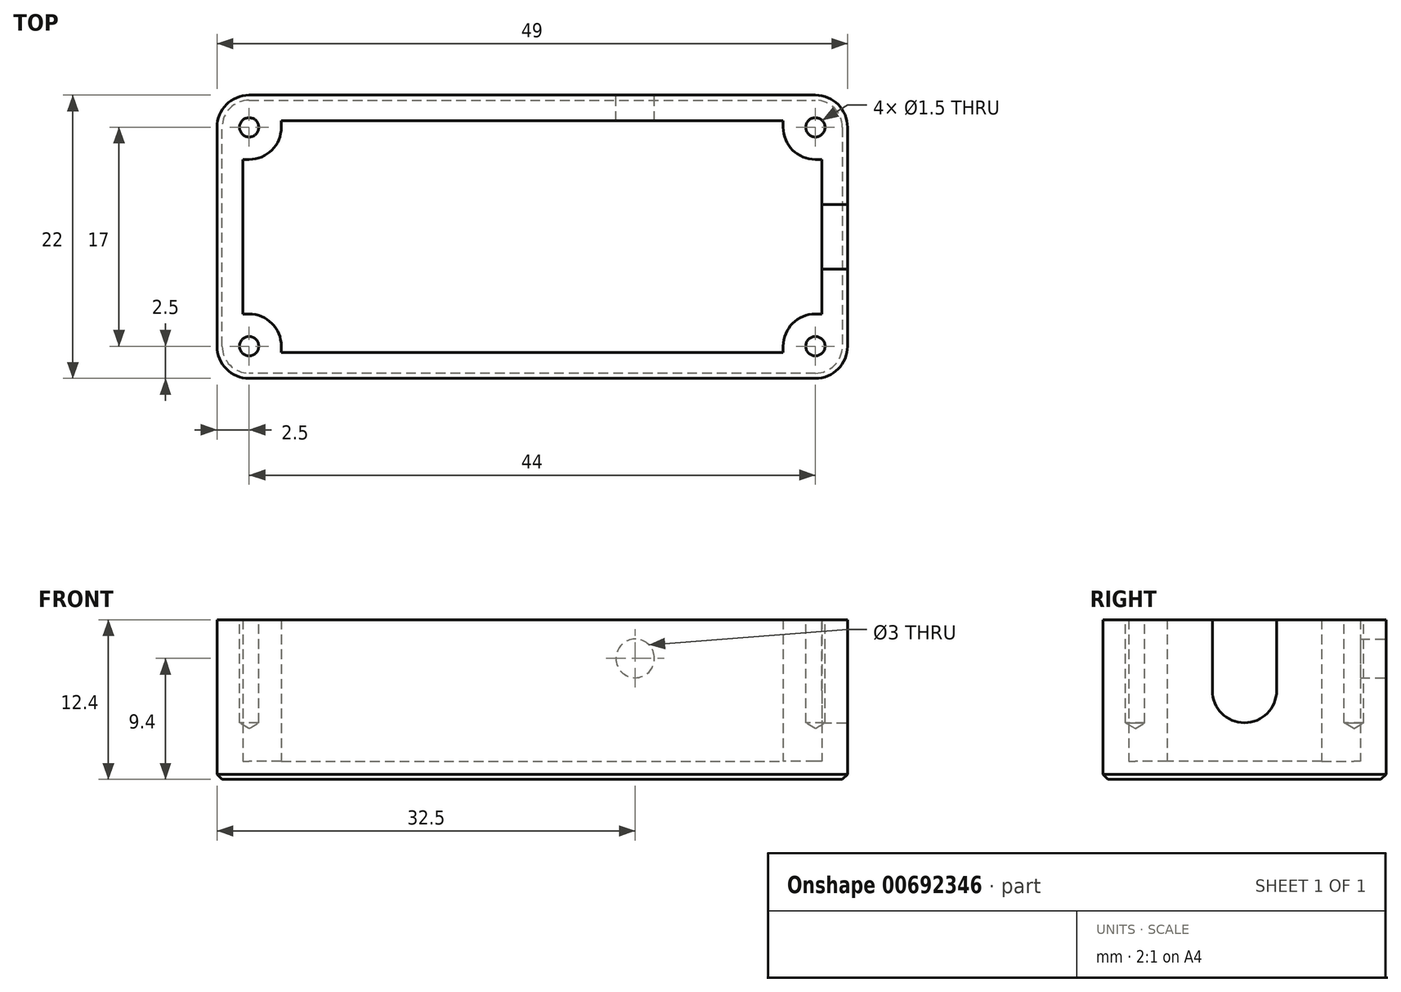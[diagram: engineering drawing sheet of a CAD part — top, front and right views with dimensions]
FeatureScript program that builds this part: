
annotation { "Feature Type Name" : "Feature", "Feature Type Description" : "" }
export const myFeature = defineFeature(function(context is Context, id is Id, definition is map)
    precondition{}
    {
        {
            var Q0;
            Q0=qCreatedBy(makeId("Top.planeOp"),FACE);
            var sketch = newSketch(context, id + "F0", { "sketchPlane" : qUnion([Q0])});
            skLineSegment(sketch, "E0.bottom", {"start": v(0, 18) * mm, "end": v(45, 18) * mm});
            skLineSegment(sketch, "E0.top", {"start": v(0, 0) * mm, "end": v(45, 0) * mm});
            skLineSegment(sketch, "E0.left", {"start": v(0, 18) * mm, "end": v(0, 0) * mm});
            skLineSegment(sketch, "E0.right", {"start": v(45, 18) * mm, "end": v(45, 0) * mm});
            skLineSegment(sketch, "E1.0", {"start": v(47, 20) * mm, "end": v(47, -2) * mm});
            skLineSegment(sketch, "E1.1", {"start": v(-2, 20) * mm, "end": v(47, 20) * mm});
            skLineSegment(sketch, "E1.2", {"start": v(-2, 20) * mm, "end": v(-2, -2) * mm});
            skLineSegment(sketch, "E1.3", {"start": v(-2, -2) * mm, "end": v(47, -2) * mm});
            skSolve(sketch);
        }
        {
            var Q0;
            Q0 = qSketchRegion(id + "F0", true);
            extrude(context, id + "F1", {"entities" : qUnion([Q0]), "depth" : 11 * mm, "offsetDistance" : 25 * mm});
        }
        {
            var Q0;
            Q0=makeQuery(id+"F1.opExtrude","CAP_FACE",FACE,{"disambiguationData":[OSD([sQuery(id+"F0.wireOp",EDGE,"E0.bottom"),sQuery(id+"F0.wireOp",EDGE,"E0.top"),sQuery(id+"F0.wireOp",EDGE,"E0.left"),sQuery(id+"F0.wireOp",EDGE,"E0.right"),sQuery(id+"F0.wireOp",EDGE,"E1.0"),sQuery(id+"F0.wireOp",EDGE,"E1.1"),sQuery(id+"F0.wireOp",EDGE,"E1.2"),sQuery(id+"F0.wireOp",EDGE,"E1.3")])],"isStart":true});
            var sketch = newSketch(context, id + "F2", { "sketchPlane" : qUnion([Q0])});
            skLineSegment(sketch, "E2.0", {"start": v(-2, -20) * mm, "end": v(47, -20) * mm});
            skLineSegment(sketch, "E3.0", {"start": v(-2, -20) * mm, "end": v(-2, 2) * mm});
            skLineSegment(sketch, "E3.1", {"start": v(-2, 2) * mm, "end": v(47, 2) * mm});
            skLineSegment(sketch, "E3.2", {"start": v(47, -20) * mm, "end": v(47, 2) * mm});
            skSolve(sketch);
        }
        {
            var Q0;
            Q0 = qSketchRegion(id + "F2", true);
            extrude(context, id + "F3", {"entities" : qUnion([Q0]), "operationType" : NewBodyOperationType.ADD, "depth" : 1.4 * mm, "offsetDistance" : 25 * mm});
        }
        {
            var Q0;
            Q0=makeQuery(id+"F3.boolean.opBoolean","MERGE",FACE,{"derivedFrom":[makeQuery(id+"F1.opExtrude","SWEPT_FACE",FACE,{"disambiguationData":[OSD([sQuery(id+"F0.wireOp",EDGE,"E1.0")])]}),makeQuery(id+"F3.opExtrude","SWEPT_FACE",FACE,{"disambiguationData":[OSD([sQuery(id+"F2.wireOp",EDGE,"E3.2")])]})]});
            var sketch = newSketch(context, id + "F4", { "sketchPlane" : qUnion([Q0])});
            skLineSegment(sketch, "E4.bottom", {"start": v(6.5, 11) * mm, "end": v(11.5, 11) * mm});
            skLineSegment(sketch, "E4.top", {"start": v(6.5, 3) * mm, "end": v(11.5, 3) * mm});
            skLineSegment(sketch, "E4.left", {"start": v(6.5, 11) * mm, "end": v(6.5, 3) * mm});
            skLineSegment(sketch, "E4.right", {"start": v(11.5, 11) * mm, "end": v(11.5, 3) * mm});
            skLineSegment(sketch, "E5", {"start": v(9, 11) * mm, "end": v(9, 3) * mm, "construction": true});
            skSolve(sketch);
        }
        {
            var Q0;
            Q0 = qSketchRegion(id + "F4", true);
            extrude(context, id + "F5", {"entities" : qUnion([Q0]), "operationType" : NewBodyOperationType.REMOVE, "endBound" : BoundingType.UP_TO_NEXT, "oppositeDirection" : true, "depth" : 25 * mm, "offsetDistance" : 25 * mm});
        }
        {
            var Q0;
            Q0=makeQuery(id+"F3.boolean.opBoolean","MERGE",FACE,{"derivedFrom":[makeQuery(id+"F1.opExtrude","SWEPT_FACE",FACE,{"disambiguationData":[OSD([sQuery(id+"F0.wireOp",EDGE,"E1.1")])]}),makeQuery(id+"F3.opExtrude","SWEPT_FACE",FACE,{"disambiguationData":[OSD([sQuery(id+"F2.wireOp",EDGE,"E2.0")])]})]});
            var sketch = newSketch(context, id + "F6", { "sketchPlane" : qUnion([Q0])});
            skCircle(sketch, "E6", {"center": v(-30.5, 8) * mm, "radius": 1.5 * mm});
            skSolve(sketch);
        }
        {
            var Q0;
            Q0 = qSketchRegion(id + "F6", true);
            extrude(context, id + "F7", {"entities" : qUnion([Q0]), "operationType" : NewBodyOperationType.REMOVE, "endBound" : BoundingType.UP_TO_NEXT, "oppositeDirection" : true, "depth" : 25 * mm, "offsetDistance" : 25 * mm});
        }
        {
            var Q0;
            Q0=makeQuery(id+"F3.opExtrude","CAP_FACE",FACE,{"disambiguationData":[OSD([sQuery(id+"F2.wireOp",EDGE,"E2.0"),sQuery(id+"F2.wireOp",EDGE,"E3.0"),sQuery(id+"F2.wireOp",EDGE,"E3.1"),sQuery(id+"F2.wireOp",EDGE,"E3.2")])],"isStart":true});
            var sketch = newSketch(context, id + "F8", { "sketchPlane" : qUnion([Q0])});
            skLineSegment(sketch, "E7.bottom", {"start": v(0, 0) * mm, "end": v(3, 0) * mm});
            skLineSegment(sketch, "E7.top", {"start": v(0, 3) * mm, "end": v(3, 3) * mm});
            skLineSegment(sketch, "E7.left", {"start": v(0, 0) * mm, "end": v(0, 3) * mm});
            skLineSegment(sketch, "E7.right", {"start": v(3, 0) * mm, "end": v(3, 3) * mm});
            skLineSegment(sketch, "E8", {"start": v(0, 9) * mm, "end": v(19.5, 9) * mm, "construction": true});
            skLineSegment(sketch, "E9", {"start": v(22.5, 0) * mm, "end": v(22.5, 9.33) * mm, "construction": true});
            skLineSegment(sketch, "E10.MirrorCS", {"start": v(45, 0) * mm, "end": v(42, 0) * mm});
            skLineSegment(sketch, "E11.MirrorCS", {"start": v(45, 3) * mm, "end": v(42, 3) * mm});
            skLineSegment(sketch, "E12.MirrorCS", {"start": v(45, 0) * mm, "end": v(45, 3) * mm});
            skLineSegment(sketch, "E13.MirrorCS", {"start": v(42, 0) * mm, "end": v(42, 3) * mm});
            skLineSegment(sketch, "E14.MirrorCS", {"start": v(3, 18) * mm, "end": v(3, 15) * mm});
            skLineSegment(sketch, "E15.MirrorCS", {"start": v(0, 18) * mm, "end": v(0, 15) * mm});
            skLineSegment(sketch, "E16.MirrorCS", {"start": v(0, 18) * mm, "end": v(3, 18) * mm});
            skLineSegment(sketch, "E17.MirrorCS", {"start": v(0, 15) * mm, "end": v(3, 15) * mm});
            skLineSegment(sketch, "E18.MirrorCS", {"start": v(45, 18) * mm, "end": v(42, 18) * mm});
            skLineSegment(sketch, "E19.MirrorCS", {"start": v(42, 18) * mm, "end": v(42, 15) * mm});
            skLineSegment(sketch, "E20.MirrorCS", {"start": v(45, 18) * mm, "end": v(45, 15) * mm});
            skLineSegment(sketch, "E21.MirrorCS", {"start": v(45, 15) * mm, "end": v(42, 15) * mm});
            skSolve(sketch);
        }
        {
            var Q0;
            Q0 = qSketchRegion(id + "F8", true);
            var Q1;
            Q1=makeQuery(id+"F1.opExtrude","CAP_FACE",FACE,{"disambiguationData":[OSD([sQuery(id+"F0.wireOp",EDGE,"E0.bottom"),sQuery(id+"F0.wireOp",EDGE,"E0.top"),sQuery(id+"F0.wireOp",EDGE,"E0.left"),sQuery(id+"F0.wireOp",EDGE,"E0.right"),sQuery(id+"F0.wireOp",EDGE,"E1.0"),sQuery(id+"F0.wireOp",EDGE,"E1.1"),sQuery(id+"F0.wireOp",EDGE,"E1.2"),sQuery(id+"F0.wireOp",EDGE,"E1.3")])],"isStart":false});
            extrude(context, id + "F9", {"entities" : qUnion([Q0]), "operationType" : NewBodyOperationType.ADD, "endBound" : BoundingType.UP_TO_SURFACE, "depth" : 25 * mm, "endBoundEntityFace" : qUnion([Q1]), "offsetDistance" : 25 * mm});
        }
        {
            var Q0;
            Q0=makeQuery(id+"F9.opExtrude","SWEPT_EDGE",EDGE,{"disambiguationData":[OSD([sQuery(id+"F8.wireOp",EDGE,"E13.MirrorCS"),sQuery(id+"F8.wireOp",EDGE,"E11.MirrorCS")])]});
            var Q1;
            Q1=makeQuery(id+"F9.opExtrude","SWEPT_EDGE",EDGE,{"disambiguationData":[OSD([sQuery(id+"F8.wireOp",EDGE,"E21.MirrorCS"),sQuery(id+"F8.wireOp",EDGE,"E19.MirrorCS")])]});
            var Q2;
            Q2=makeQuery(id+"F9.opExtrude","SWEPT_EDGE",EDGE,{"disambiguationData":[OSD([sQuery(id+"F8.wireOp",EDGE,"E7.top"),sQuery(id+"F8.wireOp",EDGE,"E7.right")])]});
            var Q3;
            Q3=makeQuery(id+"F9.opExtrude","SWEPT_EDGE",EDGE,{"disambiguationData":[OSD([sQuery(id+"F8.wireOp",EDGE,"E14.MirrorCS"),sQuery(id+"F8.wireOp",EDGE,"E17.MirrorCS")])]});
            fillet(context, id + "F10", {"entities" : qUnion([Q0, Q1, Q2, Q3]), "radius" : 2.5 * mm, "tangentPropagation" : true, "allowEdgeOverflow" : false});
        }
        {
            var Q0;
            Q0=makeQuery(id+"F3.boolean.opBoolean","MERGE",EDGE,{"derivedFrom":[makeQuery(id+"F1.opExtrude","SWEPT_EDGE",EDGE,{"disambiguationData":[OSD([sQuery(id+"F0.wireOp",EDGE,"E1.0"),sQuery(id+"F0.wireOp",EDGE,"E1.3")])]}),makeQuery(id+"F3.opExtrude","SWEPT_EDGE",EDGE,{"disambiguationData":[OSD([sQuery(id+"F2.wireOp",EDGE,"E3.1"),sQuery(id+"F2.wireOp",EDGE,"E3.2")])]})]});
            var Q1;
            Q1=makeQuery(id+"F3.boolean.opBoolean","MERGE",EDGE,{"derivedFrom":[makeQuery(id+"F1.opExtrude","SWEPT_EDGE",EDGE,{"disambiguationData":[OSD([sQuery(id+"F0.wireOp",EDGE,"E1.0"),sQuery(id+"F0.wireOp",EDGE,"E1.1")])]}),makeQuery(id+"F3.opExtrude","SWEPT_EDGE",EDGE,{"disambiguationData":[OSD([sQuery(id+"F2.wireOp",EDGE,"E2.0"),sQuery(id+"F2.wireOp",EDGE,"E3.2")])]})]});
            var Q2;
            Q2=makeQuery(id+"F3.boolean.opBoolean","MERGE",EDGE,{"derivedFrom":[makeQuery(id+"F1.opExtrude","SWEPT_EDGE",EDGE,{"disambiguationData":[OSD([sQuery(id+"F0.wireOp",EDGE,"E1.1"),sQuery(id+"F0.wireOp",EDGE,"E1.2")])]}),makeQuery(id+"F3.opExtrude","SWEPT_EDGE",EDGE,{"disambiguationData":[OSD([sQuery(id+"F2.wireOp",EDGE,"E2.0"),sQuery(id+"F2.wireOp",EDGE,"E3.0")])]})]});
            var Q3;
            Q3=makeQuery(id+"F3.boolean.opBoolean","MERGE",EDGE,{"derivedFrom":[makeQuery(id+"F1.opExtrude","SWEPT_EDGE",EDGE,{"disambiguationData":[OSD([sQuery(id+"F0.wireOp",EDGE,"E1.2"),sQuery(id+"F0.wireOp",EDGE,"E1.3")])]}),makeQuery(id+"F3.opExtrude","SWEPT_EDGE",EDGE,{"disambiguationData":[OSD([sQuery(id+"F2.wireOp",EDGE,"E3.0"),sQuery(id+"F2.wireOp",EDGE,"E3.1")])]})]});
            fillet(context, id + "F11", {"entities" : qUnion([Q0, Q1, Q2, Q3]), "radius" : 2.5 * mm, "tangentPropagation" : true, "allowEdgeOverflow" : false});
        }
        {
            var Q0;
            Q0=makeQuery(id+"F5.boolean.opBoolean","COPY",EDGE,{"derivedFrom":makeQuery(id+"F5.opExtrude","SWEPT_EDGE",EDGE,{"disambiguationData":[OSD([sQuery(id+"F4.wireOp",EDGE,"E4.top"),sQuery(id+"F4.wireOp",EDGE,"E4.right")])]})});
            var Q1;
            Q1=makeQuery(id+"F5.boolean.opBoolean","COPY",EDGE,{"derivedFrom":makeQuery(id+"F5.opExtrude","SWEPT_EDGE",EDGE,{"disambiguationData":[OSD([sQuery(id+"F4.wireOp",EDGE,"E4.top"),sQuery(id+"F4.wireOp",EDGE,"E4.left")])]})});
            fillet(context, id + "F12", {"entities" : qUnion([Q0, Q1]), "radius" : 2.5 * mm, "tangentPropagation" : true, "allowEdgeOverflow" : false});
        }
        {
            var Q0;
            {var subQ0=sQuery(id+"F0.wireOp",EDGE,"E1.3");var subQ1=sQuery(id+"F0.wireOp",EDGE,"E1.2");var subQ2=sQuery(id+"F0.wireOp",EDGE,"E1.1");var subQ3=sQuery(id+"F0.wireOp",EDGE,"E1.0");var subQ4=sQuery(id+"F0.wireOp",EDGE,"E0.right");var subQ5=sQuery(id+"F0.wireOp",EDGE,"E0.left");var subQ6=sQuery(id+"F0.wireOp",EDGE,"E0.top");var subQ7=sQuery(id+"F0.wireOp",EDGE,"E0.bottom");Q0=makeQuery(id+"F9.boolean.opBoolean","MERGE",FACE,{"derivedFrom":[makeQuery(id+"F1.opExtrude","CAP_FACE",FACE,{"disambiguationData":[OSD([subQ7,subQ6,subQ5,subQ4,subQ3,subQ2,subQ1,subQ0])],"isStart":false}),makeQuery(id+"F9.opExtrude","CAP_FACE",FACE,{"disambiguationData":[OSD([subQ7,subQ6,subQ5,subQ4,subQ3,subQ2,subQ1,subQ0]),OD(0.0)],"isStart":false}),makeQuery(id+"F9.opExtrude","CAP_FACE",FACE,{"disambiguationData":[OSD([subQ7,subQ6,subQ5,subQ4,subQ3,subQ2,subQ1,subQ0]),OD(1.0)],"isStart":false}),makeQuery(id+"F9.opExtrude","CAP_FACE",FACE,{"disambiguationData":[OSD([subQ7,subQ6,subQ5,subQ4,subQ3,subQ2,subQ1,subQ0]),OD(2.0)],"isStart":false}),makeQuery(id+"F9.opExtrude","CAP_FACE",FACE,{"disambiguationData":[OSD([subQ7,subQ6,subQ5,subQ4,subQ3,subQ2,subQ1,subQ0]),OD(3.0)],"isStart":false})]});}
            var sketch = newSketch(context, id + "F13", { "sketchPlane" : qUnion([Q0])});
            skPoint(sketch, "E22", {"position": v(44.5, 17.5) * mm});
            skPoint(sketch, "E23", {"position": v(0.5, 17.5) * mm});
            skPoint(sketch, "E24", {"position": v(44.5, 0.5) * mm});
            skPoint(sketch, "E25", {"position": v(0.5, 0.5) * mm});
            skSolve(sketch);
        }
        {
            var Q0;
            Q0=sQuery(id+"F13.wireOp",VERTEX,"E22");
            var Q1;
            Q1=sQuery(id+"F13.wireOp",VERTEX,"E24");
            var Q2;
            Q2=sQuery(id+"F13.wireOp",VERTEX,"E25");
            var Q3;
            Q3=sQuery(id+"F13.wireOp",VERTEX,"E23");
            var Q4;
            Q4=makeQuery(id+"F1.opExtrude","SWEPT_BODY",BODY,{"disambiguationData":[OSD([sQuery(id+"F0.wireOp",EDGE,"E0.bottom"),sQuery(id+"F0.wireOp",EDGE,"E0.top"),sQuery(id+"F0.wireOp",EDGE,"E0.left"),sQuery(id+"F0.wireOp",EDGE,"E0.right"),sQuery(id+"F0.wireOp",EDGE,"E1.0"),sQuery(id+"F0.wireOp",EDGE,"E1.1"),sQuery(id+"F0.wireOp",EDGE,"E1.2"),sQuery(id+"F0.wireOp",EDGE,"E1.3")])]});
            hole(context, id + "F14", {"style" : HoleStyle.SIMPLE, "endStyle" : HoleEndStyle.BLIND, "holeDiameter" : 1.5 * mm, "majorDiameter" : 5 * mm, "holeDepth" : 8 * mm, "isTappedThrough" : true, "tappedDepth" : 12 * mm, "tapClearance" : 3, "locations" : qUnion([Q0, Q1, Q2, Q3]), "scope" : qUnion([Q4])});
        }
        {
            var Q0;
            Q0=makeQuery(id+"F3.opExtrude","CAP_FACE",FACE,{"disambiguationData":[OSD([sQuery(id+"F2.wireOp",EDGE,"E2.0"),sQuery(id+"F2.wireOp",EDGE,"E3.0"),sQuery(id+"F2.wireOp",EDGE,"E3.1"),sQuery(id+"F2.wireOp",EDGE,"E3.2")])],"isStart":false});
            chamfer(context, id + "F15", {"entities" : qUnion([Q0]), "width" : 0.4 * mm, "tangentPropagation" : true});
        }
    });
